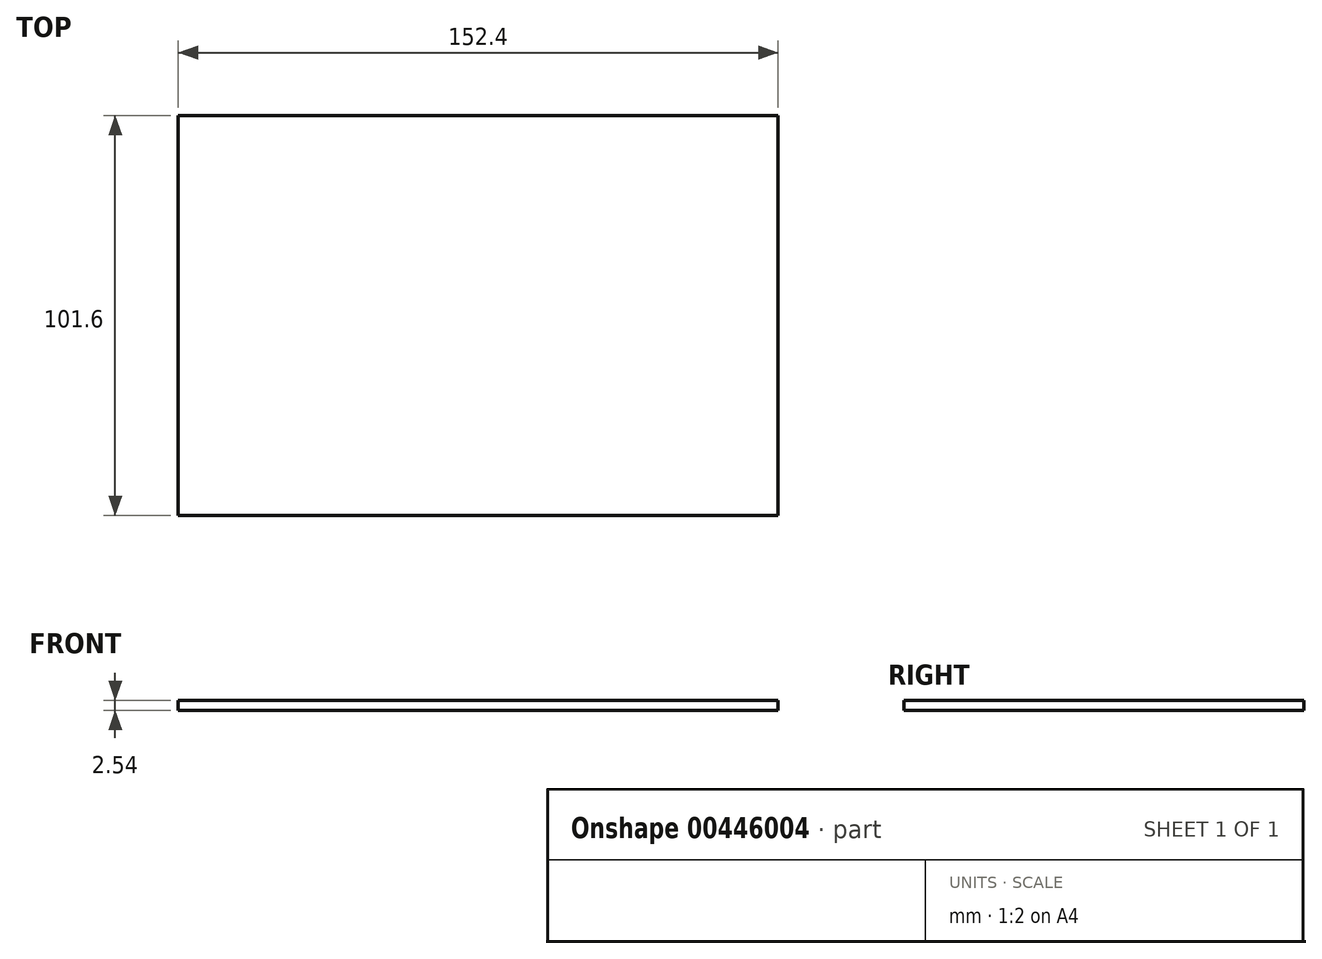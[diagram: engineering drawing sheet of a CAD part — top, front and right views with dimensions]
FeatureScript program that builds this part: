
annotation { "Feature Type Name" : "Feature", "Feature Type Description" : "" }
export const myFeature = defineFeature(function(context is Context, id is Id, definition is map)
    precondition{}
    {
        {
            var Q0;
            Q0=qCreatedBy(makeId("Top.planeOp"),FACE);
            var sketch = newSketch(context, id + "F0", { "sketchPlane" : qUnion([Q0])});
            skLineSegment(sketch, "E0.bottom", {"start": v(76.2, -50.8) * mm, "end": v(-76.2, -50.8) * mm});
            skLineSegment(sketch, "E0.top", {"start": v(76.2, 50.8) * mm, "end": v(-76.2, 50.8) * mm});
            skLineSegment(sketch, "E0.left", {"start": v(76.2, -50.8) * mm, "end": v(76.2, 50.8) * mm});
            skLineSegment(sketch, "E0.right", {"start": v(-76.2, -50.8) * mm, "end": v(-76.2, 50.8) * mm});
            skPoint(sketch, "E0.middle", {"position": v(0, 0) * mm});
            skSolve(sketch);
        }
        {
            var Q0;
            Q0 = qSketchRegion(id + "F0", true);
            extrude(context, id + "F1", {"entities" : qUnion([Q0]), "depth" : 2.54 * mm});
        }
    });
